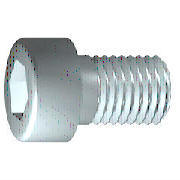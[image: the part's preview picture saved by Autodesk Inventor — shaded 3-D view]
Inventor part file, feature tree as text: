
AUTODESK INVENTOR PART (.ipt)
format: ipt  version: 2022 (Build 260153000, 153)  size: 193,024 bytes
history: native  units: mm (DEFAULTED — no unit token found)
features: sketch x2, extrude x1, plane x1, fillet x1
ambient origin geometry x7: Origin, YZ Plane, XY Plane, X Axis, Y Axis, Z Axis, Center Point
bodies: Solid1 (feature_tree), Body (feature_tree)
feature tree (5):
  extrude  "Slot"  Depth=3.0mm
  plane  "Work Plane1"
  fillet  "Fillet2"  Radius=3.0mm
  sketch  "Sketch1"  dims[d1=10.75mm d2=0.306825mm d3=3.0mm]
  sketch  "Sketch2"  dims[d4=1.3mm d5=60.0deg d6=3.0mm d7=3.0mm d8=2.886751mm d9=5.5mm d10=90.0deg d11=10.0mm d12=0.0mm d13=10.75mm d14=0.0mm d15=0.306725mm d16=0.306725mm d17=0.3mm d19=0.0mm d26=12.0mm d27=45.0deg d28=0.0mm d29=0.0mm d30=0.1mm]
